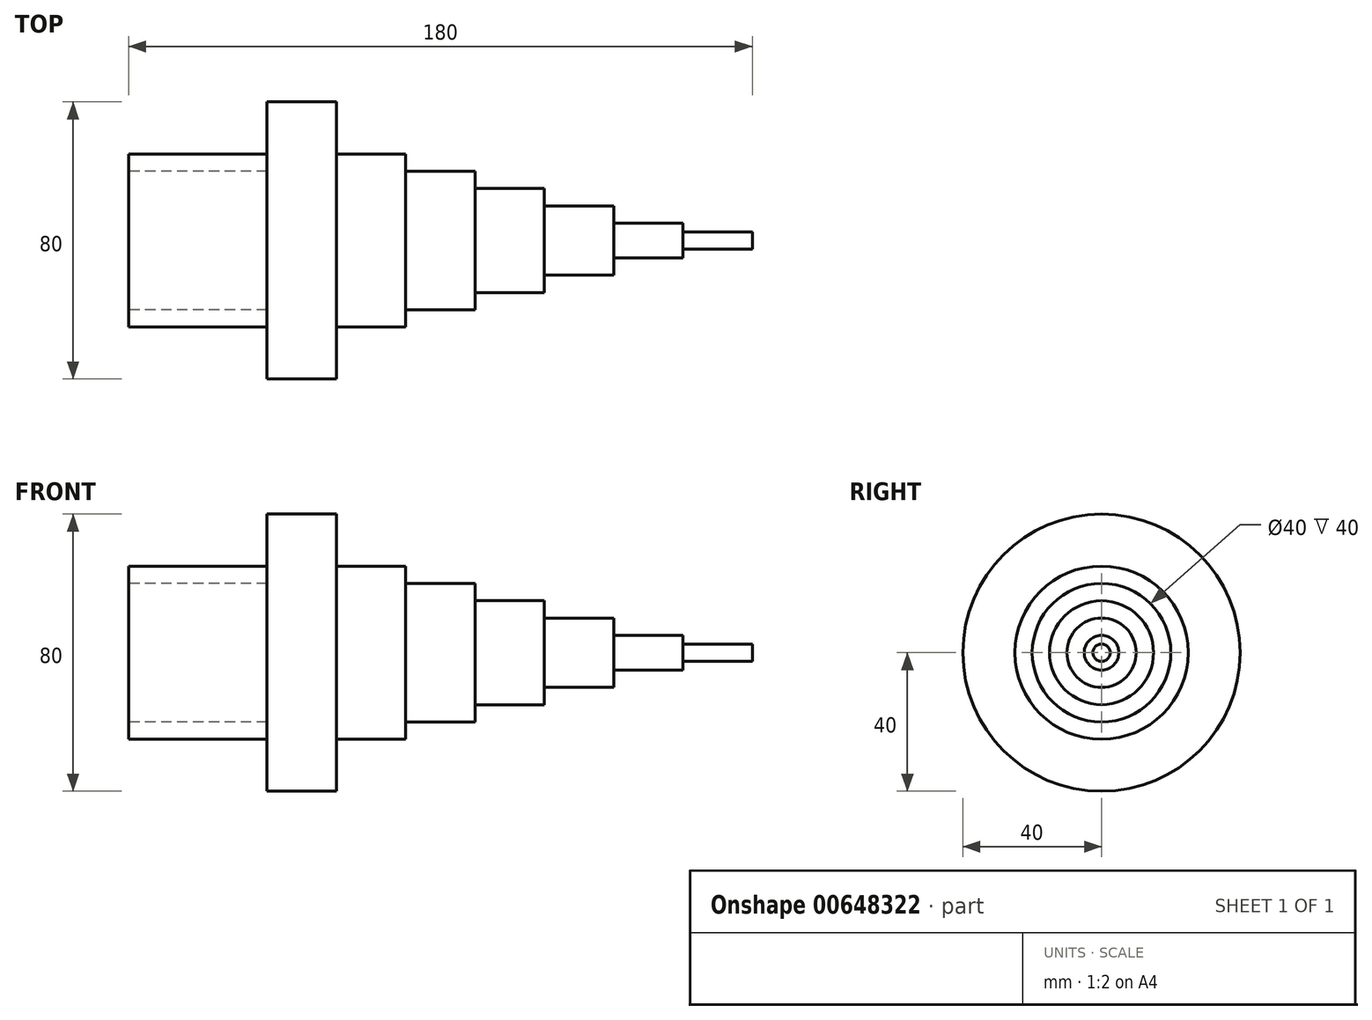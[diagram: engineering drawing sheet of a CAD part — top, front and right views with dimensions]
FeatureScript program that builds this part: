
annotation { "Feature Type Name" : "Feature", "Feature Type Description" : "" }
export const myFeature = defineFeature(function(context is Context, id is Id, definition is map)
    precondition{}
    {
        {
            var Q0;
            Q0=qCreatedBy(makeId("Front.planeOp"),FACE);
            var sketch = newSketch(context, id + "F0", { "sketchPlane" : qUnion([Q0])});
            skLineSegment(sketch, "E0", {"start": v(-140, 0) * mm, "end": v(140, 0) * mm, "construction": true});
            skLineSegment(sketch, "E1.bottom", {"start": v(0, 0) * mm, "end": v(20, 0) * mm});
            skLineSegment(sketch, "E1.top", {"start": v(0, 20) * mm, "end": v(20, 20) * mm});
            skLineSegment(sketch, "E1.left", {"start": v(0, 0) * mm, "end": v(0, 20) * mm});
            skLineSegment(sketch, "E1.right", {"start": v(20, 0) * mm, "end": v(20, 20) * mm});
            skLineSegment(sketch, "E2.bottom", {"start": v(20, 0) * mm, "end": v(40, 0) * mm});
            skLineSegment(sketch, "E2.top", {"start": v(20, 15) * mm, "end": v(40, 15) * mm});
            skLineSegment(sketch, "E2.left", {"start": v(20, 0) * mm, "end": v(20, 15) * mm});
            skLineSegment(sketch, "E2.right", {"start": v(40, 0) * mm, "end": v(40, 15) * mm});
            skLineSegment(sketch, "E3.bottom", {"start": v(40, 0) * mm, "end": v(60, 0) * mm});
            skLineSegment(sketch, "E3.top", {"start": v(40, 10) * mm, "end": v(60, 10) * mm});
            skLineSegment(sketch, "E3.left", {"start": v(40, 0) * mm, "end": v(40, 10) * mm});
            skLineSegment(sketch, "E3.right", {"start": v(60, 0) * mm, "end": v(60, 10) * mm});
            skLineSegment(sketch, "E4.bottom", {"start": v(60, 0) * mm, "end": v(80, 0) * mm});
            skLineSegment(sketch, "E4.top", {"start": v(60, 5) * mm, "end": v(80, 5) * mm});
            skLineSegment(sketch, "E4.left", {"start": v(60, 0) * mm, "end": v(60, 5) * mm});
            skLineSegment(sketch, "E4.right", {"start": v(80, 0) * mm, "end": v(80, 5) * mm});
            skLineSegment(sketch, "E5.bottom", {"start": v(80, 0) * mm, "end": v(100, 0) * mm});
            skLineSegment(sketch, "E5.top", {"start": v(80, 2.5) * mm, "end": v(100, 2.5) * mm});
            skLineSegment(sketch, "E5.left", {"start": v(80, 0) * mm, "end": v(80, 2.5) * mm});
            skLineSegment(sketch, "E5.right", {"start": v(100, 0) * mm, "end": v(100, 2.5) * mm});
            skLineSegment(sketch, "E6.bottom", {"start": v(0, 0) * mm, "end": v(-20, 0) * mm});
            skLineSegment(sketch, "E6.top", {"start": v(0, 25) * mm, "end": v(-20, 25) * mm});
            skLineSegment(sketch, "E6.left", {"start": v(0, 0) * mm, "end": v(0, 25) * mm});
            skLineSegment(sketch, "E6.right", {"start": v(-20, 0) * mm, "end": v(-20, 25) * mm});
            skLineSegment(sketch, "E7.bottom", {"start": v(-20, 0) * mm, "end": v(-40, 0) * mm});
            skLineSegment(sketch, "E7.top", {"start": v(-20, 40) * mm, "end": v(-40, 40) * mm});
            skLineSegment(sketch, "E7.left", {"start": v(-20, 0) * mm, "end": v(-20, 40) * mm});
            skLineSegment(sketch, "E7.right", {"start": v(-40, 0) * mm, "end": v(-40, 40) * mm});
            skLineSegment(sketch, "E8.bottom", {"start": v(-40, 0) * mm, "end": v(-80, 0) * mm});
            skLineSegment(sketch, "E8.top", {"start": v(-40, 25) * mm, "end": v(-80, 25) * mm});
            skLineSegment(sketch, "E8.left", {"start": v(-40, 0) * mm, "end": v(-40, 25) * mm});
            skLineSegment(sketch, "E8.right", {"start": v(-80, 0) * mm, "end": v(-80, 25) * mm});
            skSolve(sketch);
        }
        {
            var Q0;
            Q0 = qSketchRegion(id + "F0", true);
            var Q1;
            Q1=sQuery(id+"F0.wireOp",EDGE,"E0");
            revolve(context, id + "F1", {"entities" : qUnion([Q0]), "axis" : qUnion([Q1]), "revolveType" : RevolveType.FULL});
        }
        {
            var Q0;
            Q0=makeQuery(id+"F1.opRevolve","SWEPT_FACE",FACE,{"disambiguationData":[OSD([sQuery(id+"F0.wireOp",EDGE,"E8.right")])]});
            var sketch = newSketch(context, id + "F2", { "sketchPlane" : qUnion([Q0])});
            skCircle(sketch, "E9", {"center": v(0, 0) * mm, "radius": 20 * mm});
            skSolve(sketch);
        }
        {
            var Q0;
            Q0=makeQuery(id+"F2.imprint","IMPRINT",FACE,{"disambiguationData":[TD([[makeQuery(id+"F2.imprint","IMPRINT",EDGE,{"derivedFrom":sQuery(id+"F2.wireOp",EDGE,"E9")}),1.0]])]});
            extrude(context, id + "F3", {"entities" : qUnion([Q0]), "operationType" : NewBodyOperationType.REMOVE, "oppositeDirection" : true, "depth" : 40 * mm, "offsetDistance" : 25 * mm});
        }
    });
